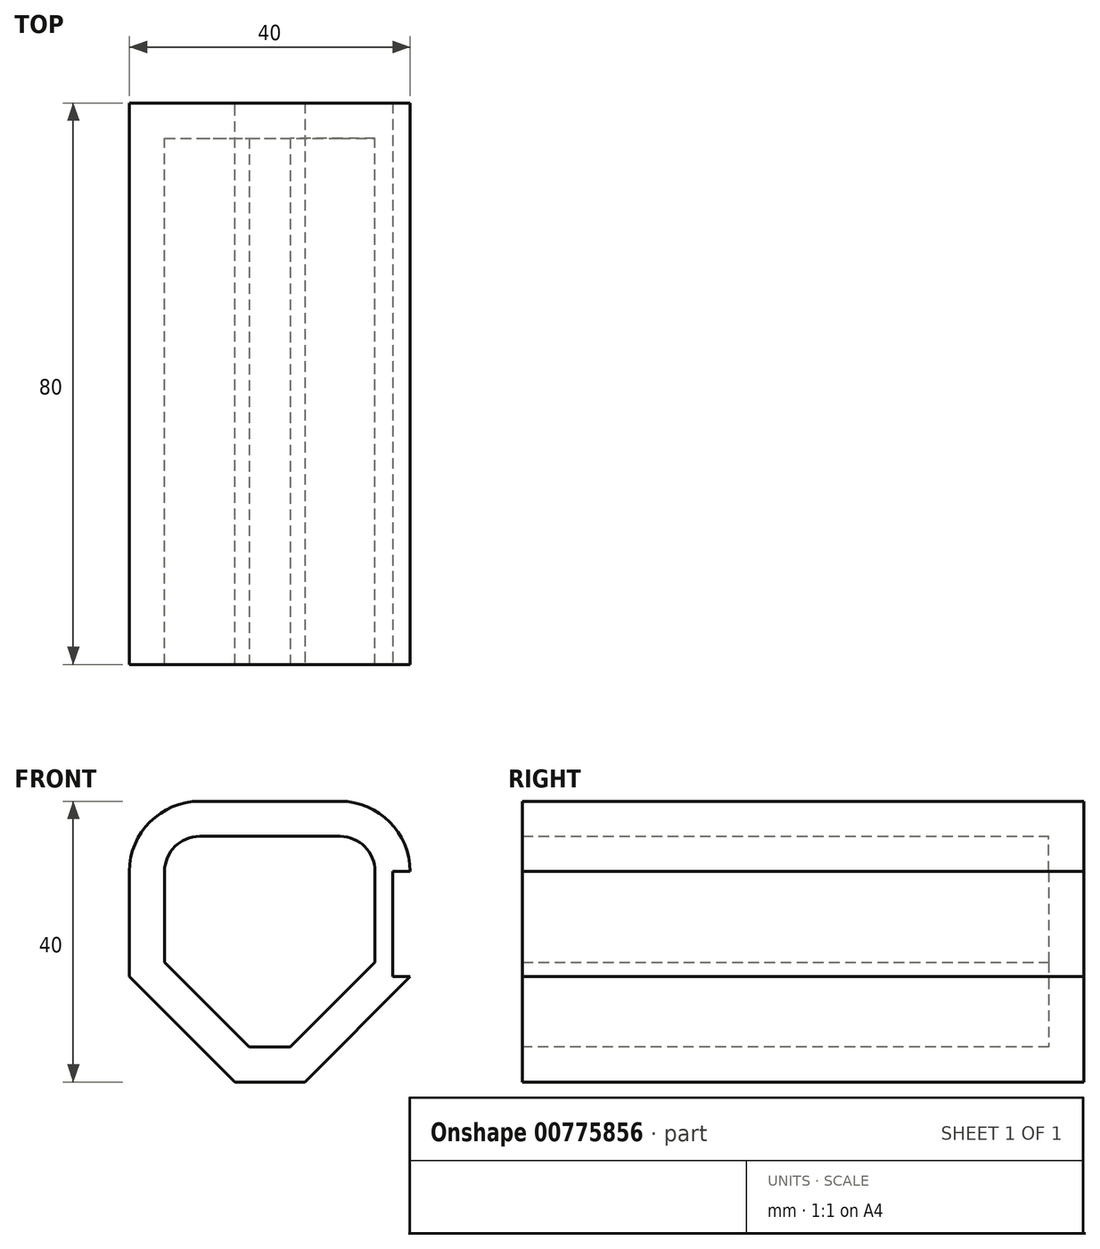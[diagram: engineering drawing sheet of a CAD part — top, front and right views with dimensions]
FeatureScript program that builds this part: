
annotation { "Feature Type Name" : "Feature", "Feature Type Description" : "" }
export const myFeature = defineFeature(function(context is Context, id is Id, definition is map)
    precondition{}
    {
        {
            var Q0;
            Q0=qCreatedBy(makeId("Top.planeOp"),FACE);
            var sketch = newSketch(context, id + "F0", { "sketchPlane" : qUnion([Q0])});
            skLineSegment(sketch, "E0.bottom", {"start": v(-20, 40) * mm, "end": v(20, 40) * mm});
            skLineSegment(sketch, "E0.top", {"start": v(-20, -40) * mm, "end": v(20, -40) * mm});
            skLineSegment(sketch, "E0.left", {"start": v(-20, 40) * mm, "end": v(-20, -40) * mm});
            skLineSegment(sketch, "E0.right", {"start": v(20, 40) * mm, "end": v(20, -40) * mm});
            skPoint(sketch, "E0.middle", {"position": v(0, 0) * mm});
            skSolve(sketch);
        }
        {
            var Q0;
            Q0 = qSketchRegion(id + "F0", true);
            extrude(context, id + "F1", {"entities" : qUnion([Q0]), "depth" : 40 * mm, "offsetDistance" : 25 * mm});
        }
        {
            var Q0;
            Q0=makeQuery(id+"F1.opExtrude","CAP_EDGE",EDGE,{"disambiguationData":[OSD([sQuery(id+"F0.wireOp",EDGE,"E0.left")])],"isStart":true});
            var Q1;
            Q1=makeQuery(id+"F1.opExtrude","CAP_EDGE",EDGE,{"disambiguationData":[OSD([sQuery(id+"F0.wireOp",EDGE,"E0.right")])],"isStart":true});
            chamfer(context, id + "F2", {"entities" : qUnion([Q0, Q1]), "width" : 15 * mm, "tangentPropagation" : true});
        }
        {
            var Q0;
            Q0=makeQuery(id+"F1.opExtrude","CAP_EDGE",EDGE,{"disambiguationData":[OSD([sQuery(id+"F0.wireOp",EDGE,"E0.left")])],"isStart":false});
            var Q1;
            Q1=makeQuery(id+"F1.opExtrude","CAP_EDGE",EDGE,{"disambiguationData":[OSD([sQuery(id+"F0.wireOp",EDGE,"E0.right")])],"isStart":false});
            fillet(context, id + "F3", {"entities" : qUnion([Q0, Q1]), "radius" : 10 * mm, "tangentPropagation" : true, "allowEdgeOverflow" : false});
        }
        {
            var Q0;
            Q0=makeQuery(id+"F1.opExtrude","SWEPT_FACE",FACE,{"disambiguationData":[OSD([sQuery(id+"F0.wireOp",EDGE,"E0.top")])]});
            shell(context, id + "F4", {"entities" : qUnion([Q0]), "thickness" : 5 * mm});
        }
        {
            var Q0;
            Q0=makeQuery(id+"F1.opExtrude","SWEPT_FACE",FACE,{"disambiguationData":[OSD([sQuery(id+"F0.wireOp",EDGE,"E0.right")])]});
            extrude(context, id + "F5", {"entities" : qUnion([Q0]), "operationType" : NewBodyOperationType.REMOVE, "oppositeDirection" : true, "depth" : 2.5 * mm, "offsetDistance" : 25 * mm});
        }
    });
